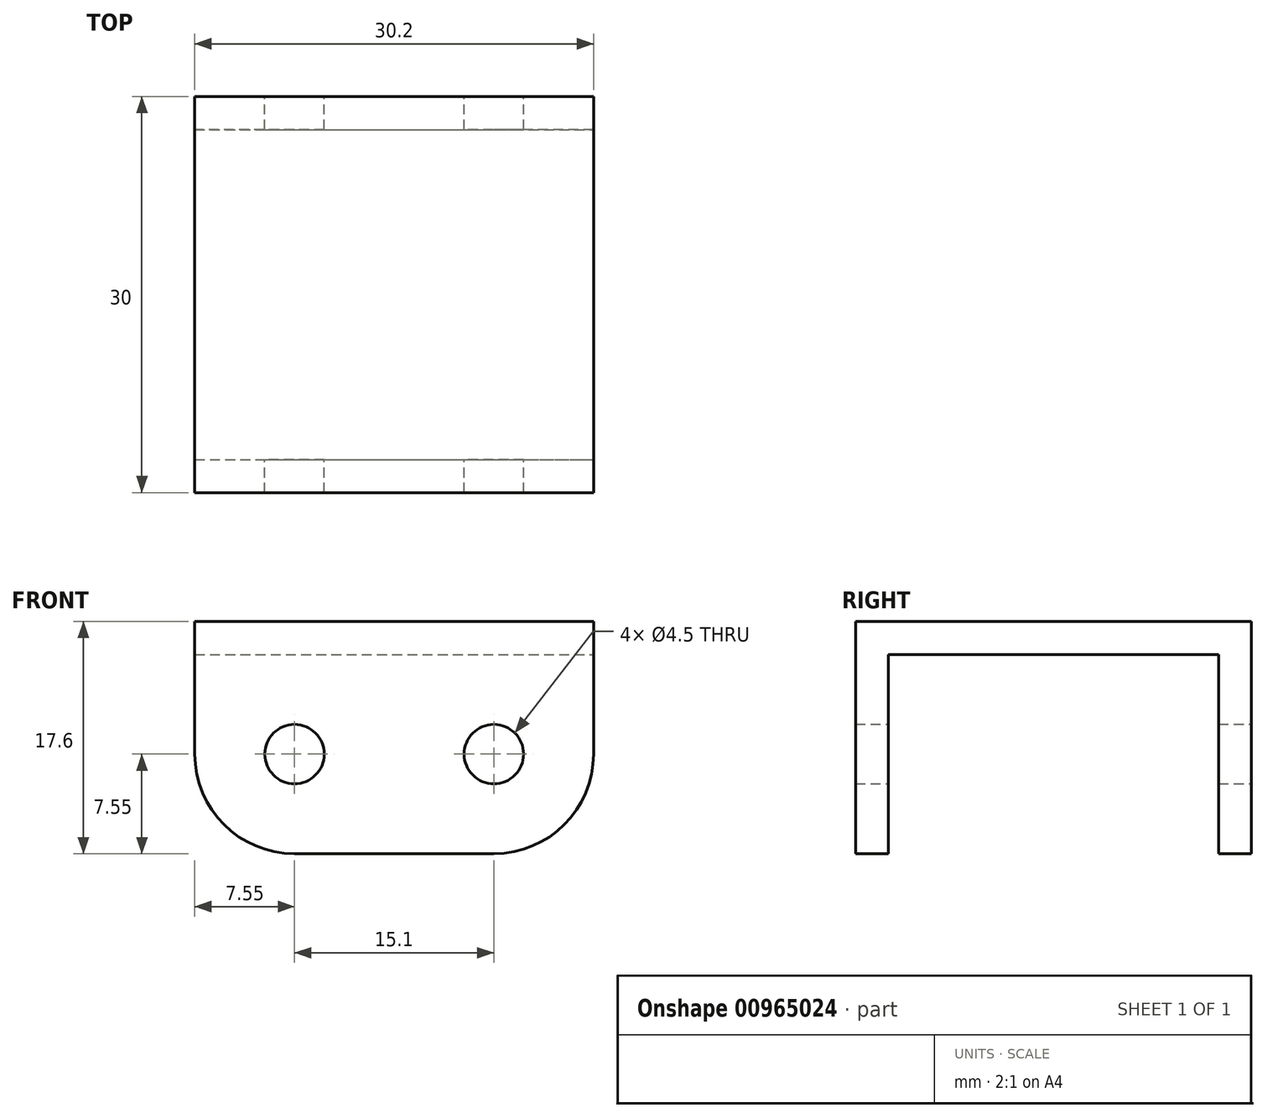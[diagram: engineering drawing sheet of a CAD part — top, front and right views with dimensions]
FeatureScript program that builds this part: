
annotation { "Feature Type Name" : "Feature", "Feature Type Description" : "" }
export const myFeature = defineFeature(function(context is Context, id is Id, definition is map)
    precondition{}
    {
        {
            var Q0;
            Q0=qCreatedBy(makeId("Front.planeOp"),FACE);
            var sketch = newSketch(context, id + "F0", { "sketchPlane" : qUnion([Q0])});
            skCircle(sketch, "E0", {"center": v(7.55, 0) * mm, "radius": 2.25 * mm});
            skCircle(sketch, "E1", {"center": v(-7.55, 0) * mm, "radius": 2.25 * mm});
            skCircle(sketch, "E2", {"center": v(-7.55, 0) * mm, "radius": 7.55 * mm});
            skCircle(sketch, "E3", {"center": v(7.55, 0) * mm, "radius": 7.55 * mm});
            skLineSegment(sketch, "E4", {"start": v(-7.55, -7.55) * mm, "end": v(7.55, -7.55) * mm});
            skLineSegment(sketch, "E5", {"start": v(-7.55, 7.55) * mm, "end": v(7.55, 7.55) * mm});
            skLineSegment(sketch, "E6", {"start": v(7.55, 7.55) * mm, "end": v(15.1, 7.55) * mm});
            skLineSegment(sketch, "E7", {"start": v(-7.55, 7.55) * mm, "end": v(-15.1, 7.55) * mm});
            skLineSegment(sketch, "E8", {"start": v(15.1, 0) * mm, "end": v(15.1, 7.55) * mm});
            skLineSegment(sketch, "E9", {"start": v(-15.1, 0) * mm, "end": v(-15.1, 7.55) * mm});
            skSolve(sketch);
        }
        {
            var Q0;
            Q0=makeQuery(id+"F0.imprint","IMPRINT",FACE,{"disambiguationData":[TD([[makeQuery(id+"F0.imprint","IMPRINT",EDGE,{"derivedFrom":sQuery(id+"F0.wireOp",EDGE,"E1")}),-1.0]])]});
            var Q1;
            {var subQ0=sQuery(id+"F0.wireOp",EDGE,"E7");Q1=makeQuery(id+"F0.imprint","IMPRINT",FACE,{"disambiguationData":[TD([[makeQuery(id+"F0.imprint","IMPRINT",EDGE,{"derivedFrom":subQ0}),1.0]])]});}
            var Q2;
            {var subQ0=sQuery(id+"F0.wireOp",EDGE,"E5");Q2=makeQuery(id+"F0.imprint","IMPRINT",FACE,{"disambiguationData":[TD([[makeQuery(id+"F0.imprint","IMPRINT",EDGE,{"derivedFrom":subQ0}),-1.0]])]});}
            var Q3;
            {var subQ0=sQuery(id+"F0.wireOp",EDGE,"E6");Q3=makeQuery(id+"F0.imprint","IMPRINT",FACE,{"disambiguationData":[TD([[makeQuery(id+"F0.imprint","IMPRINT",EDGE,{"derivedFrom":subQ0}),-1.0]])]});}
            var Q4;
            {var subQ0=sQuery(id+"F0.wireOp",EDGE,"E4");Q4=makeQuery(id+"F0.imprint","IMPRINT",FACE,{"disambiguationData":[TD([[makeQuery(id+"F0.imprint","IMPRINT",EDGE,{"derivedFrom":subQ0}),1.0]])]});}
            var Q5;
            Q5=makeQuery(id+"F0.imprint","IMPRINT",FACE,{"disambiguationData":[TD([[makeQuery(id+"F0.imprint","IMPRINT",EDGE,{"derivedFrom":sQuery(id+"F0.wireOp",EDGE,"E0")}),-1.0]])]});
            extrude(context, id + "F1", {"entities" : qUnion([Q0, Q1, Q2, Q3, Q4, Q5]), "endBound" : BoundingType.SYMMETRIC, "depth" : 30 * mm, "offsetDistance" : 25 * mm});
        }
        {
            var Q0;
            Q0=makeQuery(id+"F1.opExtrude","SWEPT_FACE",FACE,{"disambiguationData":[OSD([sQuery(id+"F0.wireOp",EDGE,"E5"),sQuery(id+"F0.wireOp",EDGE,"E6"),sQuery(id+"F0.wireOp",EDGE,"E7")])]});
            var sketch = newSketch(context, id + "F2", { "sketchPlane" : qUnion([Q0])});
            skSolve(sketch);
        }
        {
            var Q0;
            {var subQ0=sQuery(id+"F0.wireOp",EDGE,"E6");Q0=makeQuery(id+"F2.imprint","IMPRINT",FACE,{"disambiguationData":[TD([[makeQuery(id+"F2.imprint","IMPRINT",EDGE,{"derivedFrom":makeQuery(id+"F1.opExtrude","SWEPT_EDGE",EDGE,{"disambiguationData":[OSD([subQ0,sQuery(id+"F0.wireOp",EDGE,"E8")])]})}),1.0]])]});}
            extrude(context, id + "F3", {"entities" : qUnion([Q0]), "operationType" : NewBodyOperationType.ADD, "depth" : 2.5 * mm, "offsetDistance" : 25 * mm});
        }
        {
            var Q0;
            {var subQ0=sQuery(id+"F0.wireOp",EDGE,"E8");Q0=makeQuery(id+"F3.boolean.opBoolean","MERGE",FACE,{"derivedFrom":[makeQuery(id+"F1.opExtrude","SWEPT_FACE",FACE,{"disambiguationData":[OSD([subQ0])]}),makeQuery(id+"F3.opExtrude","SWEPT_FACE",FACE,{"disambiguationData":[OSD([sQuery(id+"F0.wireOp",EDGE,"E6"),subQ0])]})]});}
            var sketch = newSketch(context, id + "F4", { "sketchPlane" : qUnion([Q0])});
            skLineSegment(sketch, "E10.0.0", {"start": v(15, 0) * mm, "end": v(15, 10.05) * mm});
            skLineSegment(sketch, "E10.0.1", {"start": v(15, 10.05) * mm, "end": v(-15, 10.05) * mm});
            skLineSegment(sketch, "E10.0.2", {"start": v(-15, 10.05) * mm, "end": v(-15, 0) * mm});
            skLineSegment(sketch, "E10.0.3", {"start": v(-15, 0) * mm, "end": v(15, 0) * mm});
            skLineSegment(sketch, "E11.0.0", {"start": v(15, -7.55) * mm, "end": v(15, 0) * mm});
            skLineSegment(sketch, "E11.0.1", {"start": v(15, 0) * mm, "end": v(-15, 0) * mm});
            skLineSegment(sketch, "E11.0.2", {"start": v(-15, 0) * mm, "end": v(-15, -7.55) * mm});
            skLineSegment(sketch, "E11.0.3", {"start": v(-15, -7.55) * mm, "end": v(15, -7.55) * mm});
            skLineSegment(sketch, "E12.0", {"start": v(-12.5, 0) * mm, "end": v(-12.5, -7.55) * mm});
            skLineSegment(sketch, "E12.1", {"start": v(12.5, -7.55) * mm, "end": v(12.5, 0) * mm});
            skLineSegment(sketch, "E12.2", {"start": v(12.5, 0) * mm, "end": v(12.5, 7.55) * mm});
            skLineSegment(sketch, "E12.3", {"start": v(12.5, 7.55) * mm, "end": v(-12.5, 7.55) * mm});
            skLineSegment(sketch, "E12.4", {"start": v(-12.5, 7.55) * mm, "end": v(-12.5, 0) * mm});
            skSolve(sketch);
        }
        {
            var Q0;
            {var subQ2=sQuery(id+"F4.wireOp",EDGE,"E12.2");Q0=makeQuery(id+"F4.imprint","IMPRINT",FACE,{"disambiguationData":[TD([[makeQuery(id+"F4.imprint","IMPRINT",EDGE,{"derivedFrom":subQ2}),1.0]])]});}
            var Q1;
            {var subQ0=sQuery(id+"F4.wireOp",EDGE,"E12.0");Q1=makeQuery(id+"F4.imprint","IMPRINT",FACE,{"disambiguationData":[TD([[makeQuery(id+"F4.imprint","IMPRINT",EDGE,{"derivedFrom":subQ0}),1.0]])]});}
            extrude(context, id + "F5", {"entities" : qUnion([Q0, Q1]), "operationType" : NewBodyOperationType.REMOVE, "endBound" : BoundingType.THROUGH_ALL, "oppositeDirection" : true, "depth" : 25 * mm, "offsetDistance" : 25 * mm});
        }
    });
